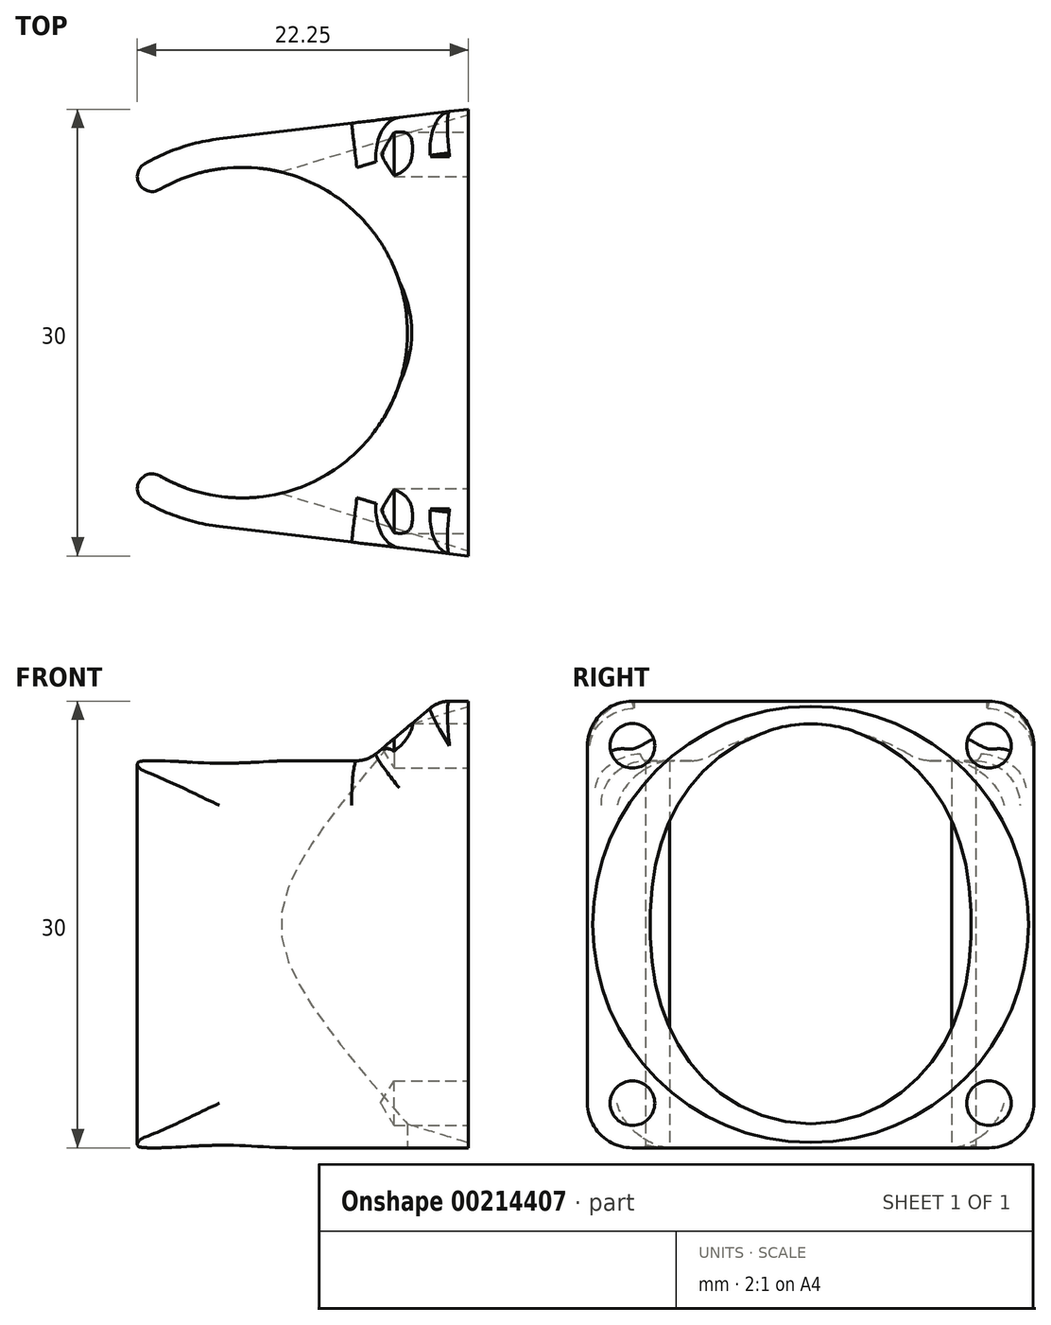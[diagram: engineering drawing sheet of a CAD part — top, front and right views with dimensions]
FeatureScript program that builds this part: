
annotation { "Feature Type Name" : "Feature", "Feature Type Description" : "" }
export const myFeature = defineFeature(function(context is Context, id is Id, definition is map)
    precondition{}
    {
        {
            var Q0;
            Q0=qCreatedBy(makeId("Top.planeOp"),FACE);
            var sketch = newSketch(context, id + "F0", { "sketchPlane" : qUnion([Q0])});
            skArc(sketch, "E0", {"start": v(-5.55, -9.61) * mm, "mid": v(11.1, 0) * mm, "end": v(-5.55, 9.61) * mm});
            skLineSegment(sketch, "E1", {"start": v(0, 0) * mm, "end": v(-11.1, 0) * mm, "construction": true});
            skLineSegment(sketch, "E2", {"start": v(0, 0) * mm, "end": v(-6.55, 11.34) * mm, "construction": true});
            skLineSegment(sketch, "E3", {"start": v(0, 0) * mm, "end": v(-6.55, -11.34) * mm, "construction": true});
            skLineSegment(sketch, "E4", {"start": v(15.2, 15) * mm, "end": v(15.2, -15) * mm});
            skArc(sketch, "E5.0", {"start": v(-1.55, 13) * mm, "mid": v(-4.13, 12.43) * mm, "end": v(-6.55, 11.34) * mm});
            skLineSegment(sketch, "E6", {"start": v(15.2, 15) * mm, "end": v(-1.55, 13) * mm});
            skLineSegment(sketch, "E7", {"start": v(15.2, -15) * mm, "end": v(-1.55, -13) * mm});
            skArc(sketch, "E8.trimOffspring", {"start": v(-6.55, -11.34) * mm, "mid": v(-4.13, -12.43) * mm, "end": v(-1.55, -13) * mm});
            skArc(sketch, "E9", {"start": v(-6.55, 11.34) * mm, "mid": v(-6.92, 9.98) * mm, "end": v(-5.55, 9.61) * mm});
            skArc(sketch, "E10", {"start": v(-5.55, -9.61) * mm, "mid": v(-6.92, -9.98) * mm, "end": v(-6.55, -11.34) * mm});
            skSolve(sketch);
        }
        {
            var Q0;
            Q0 = qSketchRegion(id + "F0", true);
            extrude(context, id + "F1", {"entities" : qUnion([Q0]), "depth" : 30 * mm});
        }
        {
            var Q0;
            Q0=qCreatedBy(makeId("Right.planeOp"),FACE);
            var sketch = newSketch(context, id + "F2", { "sketchPlane" : qUnion([Q0])});
            skLineSegment(sketch, "E11", {"start": v(0, 0) * mm, "end": v(0, 15) * mm, "construction": true});
            skCircle(sketch, "E12", {"center": v(0, 15) * mm, "radius": 10 * mm});
            skSolve(sketch);
        }
        {
            var Q0;
            Q0 = qSketchRegion(id + "F2", true);
            extrude(context, id + "F3", {"entities" : qUnion([Q0]), "operationType" : NewBodyOperationType.REMOVE, "depth" : 20 * mm, "hasDraft" : true, "draftAngle" : 17 * degree});
        }
        {
            var Q0;
            Q0=qCreatedBy(makeId("Front.planeOp"),FACE);
            var sketch = newSketch(context, id + "F4", { "sketchPlane" : qUnion([Q0])});
            skLineSegment(sketch, "E13", {"start": v(0, 0) * mm, "end": v(0, 26) * mm, "construction": true});
            skLineSegment(sketch, "E14", {"start": v(0, 26) * mm, "end": v(7.7, 26) * mm});
            skLineSegment(sketch, "E15", {"start": v(9, 26.47) * mm, "end": v(12.64, 29.53) * mm});
            skLineSegment(sketch, "E16", {"start": v(13.93, 30) * mm, "end": v(15.2, 30) * mm});
            skLineSegment(sketch, "E17", {"start": v(0, 26) * mm, "end": v(-8, 26) * mm});
            skPoint(sketch, "E18.visualSharp", {"position": v(8.43, 26) * mm});
            skArc(sketch, "E18.filletArc", {"start": v(7.7, 26) * mm, "mid": v(8.39, 26.12) * mm, "end": v(9, 26.47) * mm});
            skPoint(sketch, "E19.visualSharp", {"position": v(13.2, 30) * mm});
            skArc(sketch, "E19.filletArc", {"start": v(13.93, 30) * mm, "mid": v(13.24, 29.88) * mm, "end": v(12.64, 29.53) * mm});
            skLineSegment(sketch, "E20", {"start": v(15.2, 30) * mm, "end": v(15.2, 32) * mm});
            skLineSegment(sketch, "E21", {"start": v(15.2, 32) * mm, "end": v(-8, 32) * mm});
            skLineSegment(sketch, "E22", {"start": v(-8, 32) * mm, "end": v(-8, 26) * mm});
            skSolve(sketch);
        }
        {
            var Q0;
            Q0 = qSketchRegion(id + "F4", true);
            extrude(context, id + "F5", {"entities" : qUnion([Q0]), "operationType" : NewBodyOperationType.REMOVE, "oppositeDirection" : true, "depth" : 25 * mm});
        }
        {
            var Q0;
            Q0 = qSketchRegion(id + "F4", true);
            extrude(context, id + "F6", {"entities" : qUnion([Q0]), "operationType" : NewBodyOperationType.REMOVE, "depth" : 25 * mm});
        }
        {
            var Q0;
            Q0=makeQuery(id+"F1.opExtrude","CAP_EDGE",EDGE,{"disambiguationData":[OSD([sQuery(id+"F0.wireOp",EDGE,"E7")])],"isStart":false});
            var Q1;
            Q1=makeQuery(id+"F6.boolean.opBoolean","INTERSECT",EDGE,{"derivedFrom":[makeQuery(id+"F1.opExtrude","SWEPT_FACE",FACE,{"disambiguationData":[OSD([sQuery(id+"F0.wireOp",EDGE,"E7")])]}),makeQuery(id+"F6.opExtrude","SWEPT_FACE",FACE,{"disambiguationData":[OSD([sQuery(id+"F4.wireOp",EDGE,"E19.filletArc")])]})]});
            var Q2;
            Q2=makeQuery(id+"F6.boolean.opBoolean","INTERSECT",EDGE,{"derivedFrom":[makeQuery(id+"F1.opExtrude","SWEPT_FACE",FACE,{"disambiguationData":[OSD([sQuery(id+"F0.wireOp",EDGE,"E7")])]}),makeQuery(id+"F6.opExtrude","SWEPT_FACE",FACE,{"disambiguationData":[OSD([sQuery(id+"F4.wireOp",EDGE,"E15")])]})]});
            var Q3;
            Q3=makeQuery(id+"F6.boolean.opBoolean","INTERSECT",EDGE,{"derivedFrom":[makeQuery(id+"F1.opExtrude","SWEPT_FACE",FACE,{"disambiguationData":[OSD([sQuery(id+"F0.wireOp",EDGE,"E7")])]}),makeQuery(id+"F6.opExtrude","SWEPT_FACE",FACE,{"disambiguationData":[OSD([sQuery(id+"F4.wireOp",EDGE,"E18.filletArc")])]})]});
            var Q4;
            Q4=makeQuery(id+"F6.boolean.opBoolean","INTERSECT",EDGE,{"derivedFrom":[makeQuery(id+"F1.opExtrude","SWEPT_FACE",FACE,{"disambiguationData":[OSD([sQuery(id+"F0.wireOp",EDGE,"E7")])]}),makeQuery(id+"F6.opExtrude","SWEPT_FACE",FACE,{"disambiguationData":[OSD([sQuery(id+"F4.wireOp",EDGE,"E14"),sQuery(id+"F4.wireOp",EDGE,"E17")])]})]});
            var Q5;
            Q5=makeQuery(id+"F1.opExtrude","CAP_EDGE",EDGE,{"disambiguationData":[OSD([sQuery(id+"F0.wireOp",EDGE,"E6")])],"isStart":false});
            var Q6;
            Q6=makeQuery(id+"F5.boolean.opBoolean","INTERSECT",EDGE,{"derivedFrom":[makeQuery(id+"F1.opExtrude","SWEPT_FACE",FACE,{"disambiguationData":[OSD([sQuery(id+"F0.wireOp",EDGE,"E6")])]}),makeQuery(id+"F5.opExtrude","SWEPT_FACE",FACE,{"disambiguationData":[OSD([sQuery(id+"F4.wireOp",EDGE,"E19.filletArc")])]})]});
            var Q7;
            Q7=makeQuery(id+"F5.boolean.opBoolean","INTERSECT",EDGE,{"derivedFrom":[makeQuery(id+"F1.opExtrude","SWEPT_FACE",FACE,{"disambiguationData":[OSD([sQuery(id+"F0.wireOp",EDGE,"E6")])]}),makeQuery(id+"F5.opExtrude","SWEPT_FACE",FACE,{"disambiguationData":[OSD([sQuery(id+"F4.wireOp",EDGE,"E15")])]})]});
            var Q8;
            Q8=makeQuery(id+"F5.boolean.opBoolean","INTERSECT",EDGE,{"derivedFrom":[makeQuery(id+"F1.opExtrude","SWEPT_FACE",FACE,{"disambiguationData":[OSD([sQuery(id+"F0.wireOp",EDGE,"E6")])]}),makeQuery(id+"F5.opExtrude","SWEPT_FACE",FACE,{"disambiguationData":[OSD([sQuery(id+"F4.wireOp",EDGE,"E18.filletArc")])]})]});
            var Q9;
            Q9=makeQuery(id+"F5.boolean.opBoolean","INTERSECT",EDGE,{"derivedFrom":[makeQuery(id+"F1.opExtrude","SWEPT_FACE",FACE,{"disambiguationData":[OSD([sQuery(id+"F0.wireOp",EDGE,"E6")])]}),makeQuery(id+"F5.opExtrude","SWEPT_FACE",FACE,{"disambiguationData":[OSD([sQuery(id+"F4.wireOp",EDGE,"E14"),sQuery(id+"F4.wireOp",EDGE,"E17")])]})]});
            var Q10;
            Q10=makeQuery(id+"F1.opExtrude","CAP_EDGE",EDGE,{"disambiguationData":[OSD([sQuery(id+"F0.wireOp",EDGE,"E7")])],"isStart":true});
            var Q11;
            Q11=makeQuery(id+"F1.opExtrude","CAP_EDGE",EDGE,{"disambiguationData":[OSD([sQuery(id+"F0.wireOp",EDGE,"E6")])],"isStart":true});
            fillet(context, id + "F7", {"entities" : qUnion([Q0, Q1, Q2, Q3, Q4, Q5, Q6, Q7, Q8, Q9, Q10, Q11]), "radius" : 3 * mm, "allowEdgeOverflow" : false});
        }
        {
            var Q0;
            Q0=makeQuery(id+"F1.opExtrude","SWEPT_FACE",FACE,{"disambiguationData":[OSD([sQuery(id+"F0.wireOp",EDGE,"E4")])]});
            var sketch = newSketch(context, id + "F8", { "sketchPlane" : qUnion([Q0])});
            skPoint(sketch, "E23", {"position": v(-11.98, 3) * mm});
            skPoint(sketch, "E24", {"position": v(11.98, 3) * mm});
            skPoint(sketch, "E25", {"position": v(11.98, 27) * mm});
            skPoint(sketch, "E26", {"position": v(-11.98, 27) * mm});
            skSolve(sketch);
        }
        {
            var Q0;
            Q0=sQuery(id+"F8.wireOp",VERTEX,"E26");
            var Q1;
            Q1=sQuery(id+"F8.wireOp",VERTEX,"E25");
            var Q2;
            Q2=sQuery(id+"F8.wireOp",VERTEX,"E24");
            var Q3;
            Q3=sQuery(id+"F8.wireOp",VERTEX,"E23");
            var Q4;
            Q4=makeQuery(id+"F1.opExtrude","SWEPT_BODY",BODY,{"disambiguationData":[OSD([sQuery(id+"F0.wireOp",EDGE,"E0"),sQuery(id+"F0.wireOp",EDGE,"E4"),sQuery(id+"F0.wireOp",EDGE,"E5.0"),sQuery(id+"F0.wireOp",EDGE,"E6"),sQuery(id+"F0.wireOp",EDGE,"E7"),sQuery(id+"F0.wireOp",EDGE,"E8.trimOffspring"),sQuery(id+"F0.wireOp",EDGE,"E9"),sQuery(id+"F0.wireOp",EDGE,"E10")])]});
            hole(context, id + "F9", {"style" : HoleStyle.SIMPLE, "endStyle" : HoleEndStyle.BLIND, "standardTappedOrClearance" : lookupTablePath({ "standard" : "ISO", "size" : "3", "type" : "Drilled" }), "standardBlindInLast" : lookupTablePath({ "standard" : "ISO", "size" : "3", "type" : "Drilled" }), "holeDiameter" : 3 * mm, "holeDepth" : 5 * mm, "startFromSketch" : true, "locations" : qUnion([Q0, Q1, Q2, Q3]), "scope" : qUnion([Q4])});
        }
    });
